# Revit family: 400_ISR_GEO_slagvast_opbouw_design-armatuur
name_source: partatom
category: Lighting Fixtures
revit_build: Autodesk Revit 2013 (Build: 20121003_2115(x64)
units: mm (PartAtom-declared; Revit-internal decimal feet)

## types (3) — shared parameters
Apparent Load = 0 VA
Color Filter = 16777215
Description = GEO
Dimming Lamp Color Temperature Shift = <None>
Emit Shape Visible in Rendering = No
Emit from Circle Diameter = 610 mm
Lamp = LED
Load Classification = Other
Manufacturer = Lightronics
Model = LOD400
Photometric Web File = GEO 1-LO-1-4-110-D-O-445-230-X-X.ies
URL = http://www.lightronics.nl

## per-type parameters (varying)
| type | Tilt Angle | Wattage Comments | materiaal_boven | materiaal_links | materiaal_rechts |
| GEO I | 90.00° | 2,6 Watt | ISR_polycarbonaat grijs | ISR_polycarbonaat zwart | ISR_polycarbonaat zwart |
| GEO II | 0.00° | 6 Watt | ISR_polycarbonaat zwart | ISR_polycarbonaat grijs | ISR_polycarbonaat grijs |
| GEO III | 90.00° | 9,1 Watt | ISR_polycarbonaat grijs | ISR_polycarbonaat grijs | ISR_polycarbonaat grijs |

## geometry (parser evidence)
native form markers: Sweep x3
no freeform markers — native parametric forms only
